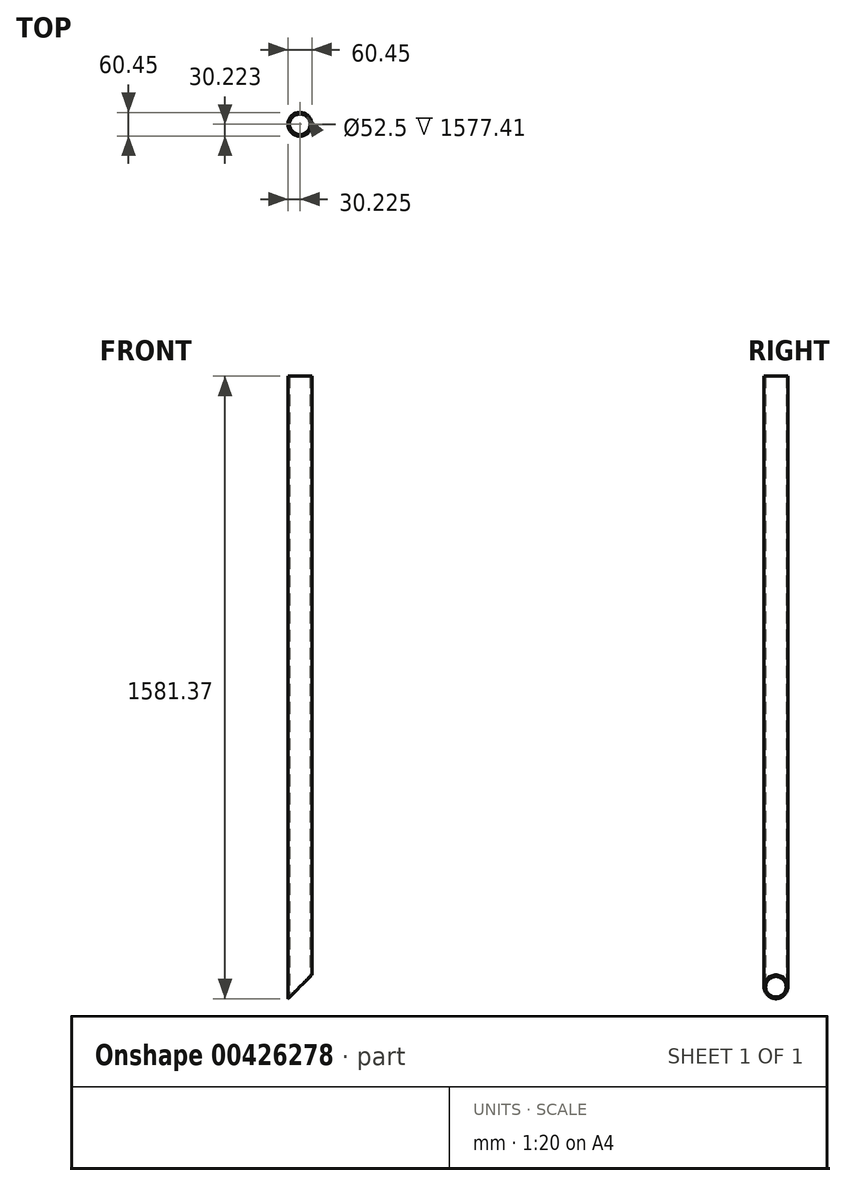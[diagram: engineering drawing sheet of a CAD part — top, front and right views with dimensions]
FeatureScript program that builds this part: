
annotation { "Feature Type Name" : "Feature", "Feature Type Description" : "" }
export const myFeature = defineFeature(function(context is Context, id is Id, definition is map)
    precondition{}
    {
        {
            var Q0;
            Q0=qCreatedBy(makeId("Top.planeOp"),FACE);
            var sketch = newSketch(context, id + "F0", { "sketchPlane" : qUnion([Q0])});
            skCircle(sketch, "E0", {"center": v(-125.82, -56.06) * mm, "radius": 30.23 * mm});
            skCircle(sketch, "E1", {"center": v(-125.82, -56.06) * mm, "radius": 26.25 * mm});
            skSolve(sketch);
        }
        {
            var Q0;
            Q0=makeQuery(id+"F0.imprint","IMPRINT",FACE,{"disambiguationData":[TD([[makeQuery(id+"F0.imprint","IMPRINT",EDGE,{"derivedFrom":sQuery(id+"F0.wireOp",EDGE,"E0")}),1.0]])]});
            extrude(context, id + "F1", {"entities" : qUnion([Q0]), "depth" : 1584.45 * mm});
        }
        {
            var Q0;
            Q0=qCreatedBy(makeId("Front.planeOp"),FACE);
            var sketch = newSketch(context, id + "F2", { "sketchPlane" : qUnion([Q0])});
            skLineSegment(sketch, "E2", {"start": v(-159.12, 0) * mm, "end": v(-89.99, 69.13) * mm});
            skLineSegment(sketch, "E3", {"start": v(-88.82, 0) * mm, "end": v(-159.12, 0) * mm});
            skLineSegment(sketch, "E4", {"start": v(-89.99, 69.13) * mm, "end": v(-88.82, 0) * mm});
            skSolve(sketch);
        }
        {
            var Q0;
            Q0=makeQuery(id+"F2.imprint","IMPRINT",FACE,{"disambiguationData":[TD([[makeQuery(id+"F2.imprint","IMPRINT",EDGE,{"derivedFrom":sQuery(id+"F2.wireOp",EDGE,"E2")}),-1.0]])]});
            extrude(context, id + "F3", {"entities" : qUnion([Q0]), "operationType" : NewBodyOperationType.REMOVE, "depth" : 103.12 * mm});
        }
    });
